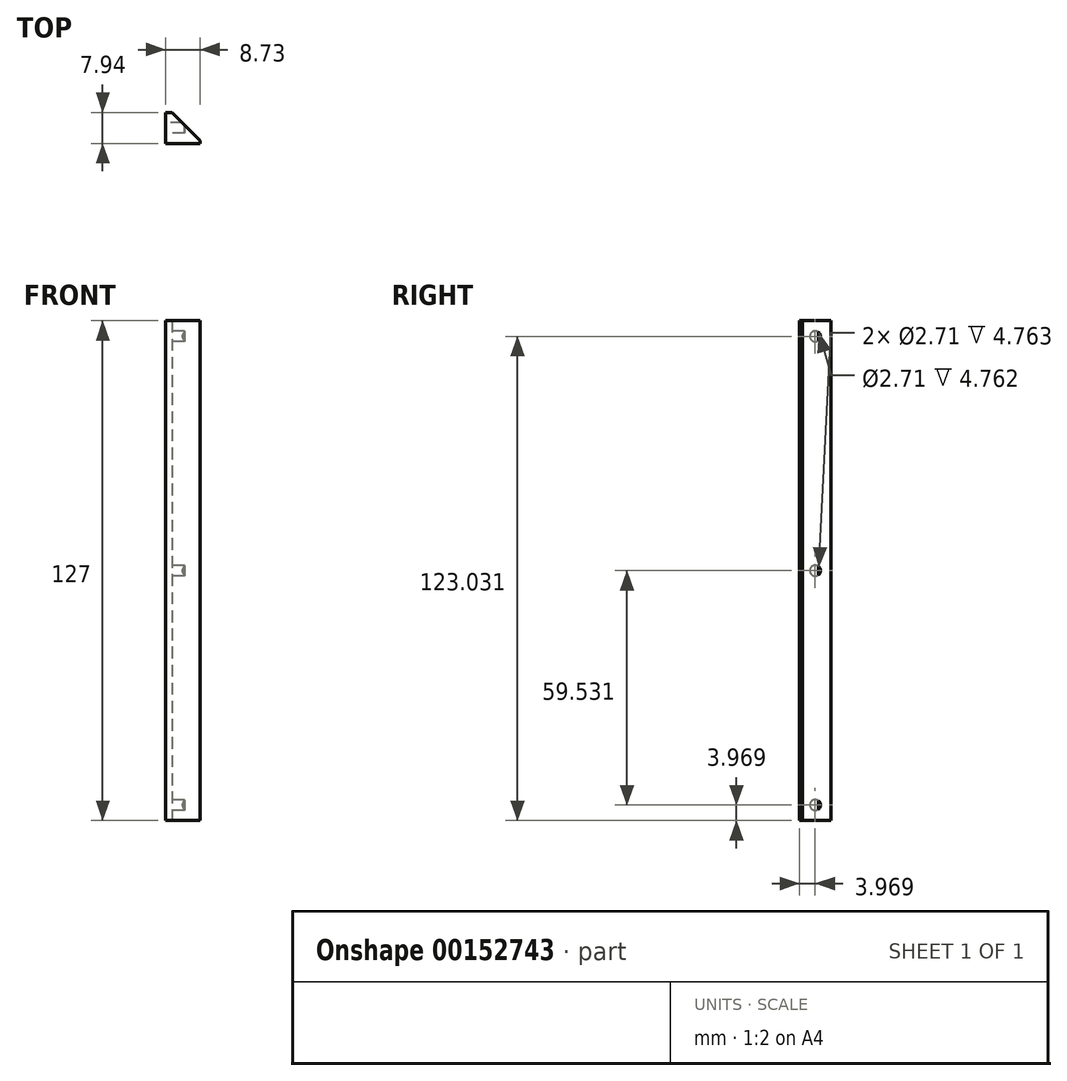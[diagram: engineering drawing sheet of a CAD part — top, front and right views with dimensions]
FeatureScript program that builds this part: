
annotation { "Feature Type Name" : "Feature", "Feature Type Description" : "" }
export const myFeature = defineFeature(function(context is Context, id is Id, definition is map)
    precondition{}
    {
        {
            var Q0;
            Q0=qCreatedBy(makeId("Top.planeOp"),FACE);
            var sketch = newSketch(context, id + "F0", { "sketchPlane" : qUnion([Q0])});
            skLineSegment(sketch, "E0", {"start": v(0, 0) * mm, "end": v(-8.73, 0) * mm});
            skLineSegment(sketch, "E1", {"start": v(0, 0) * mm, "end": v(0, 0.8) * mm});
            skLineSegment(sketch, "E2", {"start": v(0, 0.8) * mm, "end": v(-7.14, 7.94) * mm});
            skLineSegment(sketch, "E3", {"start": v(-7.14, 7.94) * mm, "end": v(-8.73, 7.94) * mm});
            skLineSegment(sketch, "E4", {"start": v(-8.73, 7.94) * mm, "end": v(-8.73, 0) * mm});
            skSolve(sketch);
        }
        {
            var Q0;
            Q0 = qSketchRegion(id + "F0", true);
            extrude(context, id + "F1", {"entities" : qUnion([Q0]), "depth" : 127 * mm});
        }
        {
            var Q0;
            Q0=makeQuery(id+"F1.opExtrude","SWEPT_FACE",FACE,{"disambiguationData":[OSD([sQuery(id+"F0.wireOp",EDGE,"E4")])]});
            var sketch = newSketch(context, id + "F2", { "sketchPlane" : qUnion([Q0])});
            skLineSegment(sketch, "E5.bottom", {"start": v(-3.97, 127) * mm, "end": v(0, 127) * mm, "construction": true});
            skLineSegment(sketch, "E5.top", {"start": v(-3.97, 123.03) * mm, "end": v(0, 123.03) * mm, "construction": true});
            skLineSegment(sketch, "E5.left", {"start": v(-3.97, 127) * mm, "end": v(-3.97, 123.03) * mm, "construction": true});
            skLineSegment(sketch, "E5.right", {"start": v(0, 127) * mm, "end": v(0, 123.03) * mm, "construction": true});
            skLineSegment(sketch, "E6.bottom", {"start": v(-3.97, 0) * mm, "end": v(0, 0) * mm, "construction": true});
            skLineSegment(sketch, "E6.top", {"start": v(-3.97, 3.97) * mm, "end": v(0, 3.97) * mm, "construction": true});
            skLineSegment(sketch, "E6.left", {"start": v(-3.97, 0) * mm, "end": v(-3.97, 3.97) * mm, "construction": true});
            skLineSegment(sketch, "E6.right", {"start": v(0, 0) * mm, "end": v(0, 3.97) * mm, "construction": true});
            skLineSegment(sketch, "E7", {"start": v(0, 63.5) * mm, "end": v(-3.97, 63.5) * mm, "construction": true});
            skCircle(sketch, "E8", {"center": v(-3.97, 123.03) * mm, "radius": 1.35 * mm});
            skCircle(sketch, "E9", {"center": v(-3.97, 63.5) * mm, "radius": 1.35 * mm});
            skCircle(sketch, "E10", {"center": v(-3.97, 3.97) * mm, "radius": 1.35 * mm});
            skSolve(sketch);
        }
        {
            var Q0;
            Q0 = qSketchRegion(id + "F2", true);
            extrude(context, id + "F3", {"entities" : qUnion([Q0]), "operationType" : NewBodyOperationType.REMOVE, "oppositeDirection" : true, "depth" : 4.76 * mm});
        }
    });
